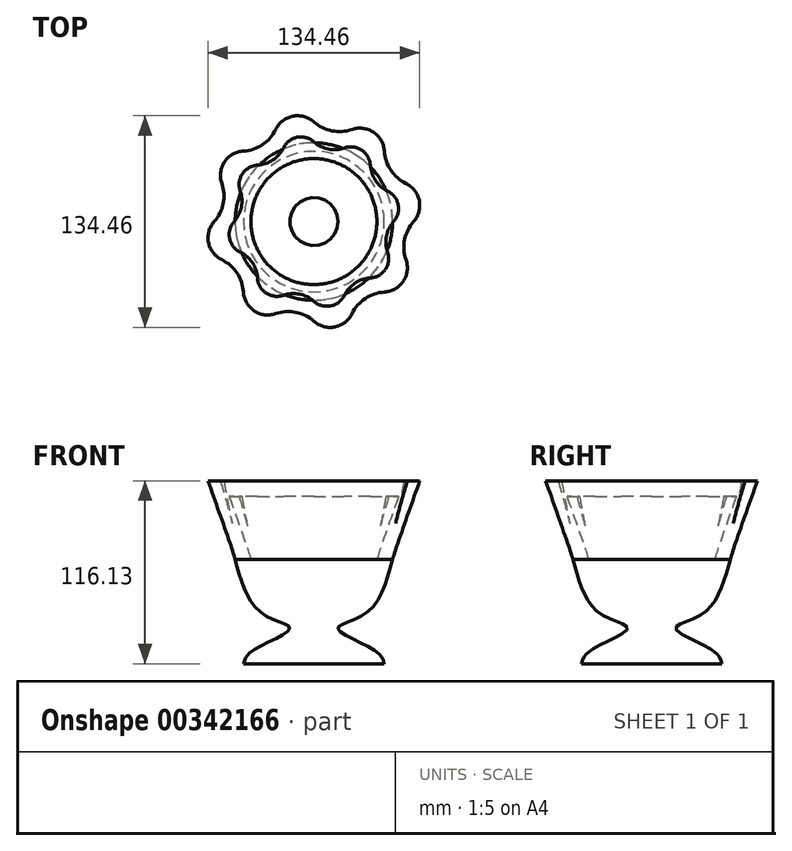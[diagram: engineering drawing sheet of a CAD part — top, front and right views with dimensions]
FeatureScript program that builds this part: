
annotation { "Feature Type Name" : "Feature", "Feature Type Description" : "" }
export const myFeature = defineFeature(function(context is Context, id is Id, definition is map)
    precondition{}
    {
        {
            var Q0;
            Q0=qCreatedBy(makeId("Top.planeOp"),FACE);
            var sketch = newSketch(context, id + "F0", { "sketchPlane" : qUnion([Q0])});
            skCircle(sketch, "E0", {"center": v(0, 0) * mm, "radius": 50 * mm});
            skSolve(sketch);
        }
        {
            var Q0;
            Q0=qCreatedBy(makeId("Front.planeOp"),FACE);
            var sketch = newSketch(context, id + "F1", { "sketchPlane" : qUnion([Q0])});
            skFitSpline(sketch, "E1", {"points": [v(-50, 0) * mm, v(-32.23, -34.65) * mm, v(-15.28, -43.73) * mm, v(-39.5, -58.26) * mm, v(-44.64, -66.13) * mm], "startDerivative": vector(35.94, -126.86) * mm, "endDerivative": vector(-11.41, -46.65) * mm});
            skLineSegment(sketch, "E2", {"start": v(-44.64, -66.13) * mm, "end": v(0, -66.13) * mm});
            skSolve(sketch);
        }
        {
            var Q0;
            Q0 = qSketchRegion(id + "F1", true);
            var Q1;
            Q1=sQuery(id+"F1.wireOp",EDGE,"E1");
            var Q2;
            Q2=sQuery(id+"F0.wireOp",EDGE,"E0");
            revolve(context, id + "F2", {"bodyType" : ToolBodyType.SURFACE, "entities" : qUnion([Q0]), "surfaceEntities" : qUnion([Q1]), "axis" : qUnion([Q2]), "revolveType" : RevolveType.FULL});
        }
        {
            var Q0;
            Q0=qCreatedBy(makeId("Top.planeOp"),FACE);
            var sketch = newSketch(context, id + "F3", { "sketchPlane" : qUnion([Q0])});
            skLineSegment(sketch, "E3", {"start": v(0, 0) * mm, "end": v(0, 63.32) * mm});
            skLineSegment(sketch, "E4.1.0", {"start": v(0, 0) * mm, "end": v(-24.23, 58.5) * mm});
            skLineSegment(sketch, "E4.2.0", {"start": v(0, 0) * mm, "end": v(-44.77, 44.77) * mm});
            skLineSegment(sketch, "E4.3.0", {"start": v(0, 0) * mm, "end": v(-58.5, 24.23) * mm});
            skLineSegment(sketch, "E4.4.0", {"start": v(0, 0) * mm, "end": v(-63.32, 0) * mm});
            skLineSegment(sketch, "E4.5.0", {"start": v(0, 0) * mm, "end": v(-58.5, -24.23) * mm});
            skLineSegment(sketch, "E4.6.0", {"start": v(0, 0) * mm, "end": v(-44.77, -44.77) * mm});
            skLineSegment(sketch, "E4.7.0", {"start": v(0, 0) * mm, "end": v(-24.23, -58.5) * mm});
            skLineSegment(sketch, "E4.8.0", {"start": v(0, 0) * mm, "end": v(0, -63.32) * mm});
            skLineSegment(sketch, "E4.9.0", {"start": v(0, 0) * mm, "end": v(24.23, -58.5) * mm});
            skLineSegment(sketch, "E4.10.0", {"start": v(0, 0) * mm, "end": v(44.77, -44.77) * mm});
            skLineSegment(sketch, "E4.11.0", {"start": v(0, 0) * mm, "end": v(58.5, -24.23) * mm});
            skLineSegment(sketch, "E4.12.0", {"start": v(0, 0) * mm, "end": v(63.32, 0) * mm});
            skLineSegment(sketch, "E4.13.0", {"start": v(0, 0) * mm, "end": v(58.5, 24.23) * mm});
            skLineSegment(sketch, "E4.14.0", {"start": v(0, 0) * mm, "end": v(44.77, 44.77) * mm});
            skLineSegment(sketch, "E4.15.0", {"start": v(0, 0) * mm, "end": v(24.23, 58.5) * mm});
            skPoint(sketch, "E4.center", {"position": v(0, 0) * mm});
            skArc(sketch, "E5", {"start": v(0, 63.32) * mm, "mid": v(-13.31, 66.93) * mm, "end": v(-24.23, 58.5) * mm});
            skArc(sketch, "E6", {"start": v(0, 63.32) * mm, "mid": v(11.46, 57.62) * mm, "end": v(24.23, 58.5) * mm});
            skArc(sketch, "E7.1.0", {"start": v(-44.77, 44.77) * mm, "mid": v(-56.74, 37.91) * mm, "end": v(-58.5, 24.23) * mm});
            skArc(sketch, "E7.1.1", {"start": v(-44.77, 44.77) * mm, "mid": v(-32.64, 48.85) * mm, "end": v(-24.23, 58.5) * mm});
            skArc(sketch, "E7.2.0", {"start": v(-63.32, 0) * mm, "mid": v(-66.93, -13.31) * mm, "end": v(-58.5, -24.23) * mm});
            skArc(sketch, "E7.2.1", {"start": v(-63.32, 0) * mm, "mid": v(-57.62, 11.46) * mm, "end": v(-58.5, 24.23) * mm});
            skArc(sketch, "E7.3.0", {"start": v(-44.77, -44.77) * mm, "mid": v(-37.91, -56.74) * mm, "end": v(-24.23, -58.5) * mm});
            skArc(sketch, "E7.3.1", {"start": v(-44.77, -44.77) * mm, "mid": v(-48.85, -32.64) * mm, "end": v(-58.5, -24.23) * mm});
            skArc(sketch, "E7.4.0", {"start": v(0, -63.32) * mm, "mid": v(13.31, -66.93) * mm, "end": v(24.23, -58.5) * mm});
            skArc(sketch, "E7.4.1", {"start": v(0, -63.32) * mm, "mid": v(-11.46, -57.62) * mm, "end": v(-24.23, -58.5) * mm});
            skArc(sketch, "E7.5.0", {"start": v(44.77, -44.77) * mm, "mid": v(56.74, -37.91) * mm, "end": v(58.5, -24.23) * mm});
            skArc(sketch, "E7.5.1", {"start": v(44.77, -44.77) * mm, "mid": v(32.64, -48.85) * mm, "end": v(24.23, -58.5) * mm});
            skArc(sketch, "E7.6.0", {"start": v(63.32, 0) * mm, "mid": v(66.93, 13.31) * mm, "end": v(58.5, 24.23) * mm});
            skArc(sketch, "E7.6.1", {"start": v(63.32, 0) * mm, "mid": v(57.62, -11.46) * mm, "end": v(58.5, -24.23) * mm});
            skArc(sketch, "E7.7.0", {"start": v(44.77, 44.77) * mm, "mid": v(37.91, 56.74) * mm, "end": v(24.23, 58.5) * mm});
            skArc(sketch, "E7.7.1", {"start": v(44.77, 44.77) * mm, "mid": v(48.85, 32.64) * mm, "end": v(58.5, 24.23) * mm});
            skSolve(sketch);
        }
        {
            var Q0;
            Q0=qCreatedBy(makeId("Top.planeOp"),FACE);
            cPlane(context, id + "F4", {"entities" : qUnion([Q0]), "cplaneType" : CPlaneType.OFFSET, "offset" : 50 * mm, "width" : 152.4 * mm, "height" : 152.4 * mm});
        }
        {
            var Q0;
            Q0=qCreatedBy(id+"F4.planeOp",FACE);
            var sketch = newSketch(context, id + "F5", { "sketchPlane" : qUnion([Q0])});
            skLineSegment(sketch, "E8.0", {"start": v(0, 0) * mm, "end": v(0, 63.32) * mm, "construction": true});
            skLineSegment(sketch, "E8.1", {"start": v(0, 0) * mm, "end": v(-24.23, 58.5) * mm, "construction": true});
            skLineSegment(sketch, "E8.2", {"start": v(0, 0) * mm, "end": v(-44.77, 44.77) * mm, "construction": true});
            skLineSegment(sketch, "E8.3", {"start": v(0, 0) * mm, "end": v(-58.5, 24.23) * mm, "construction": true});
            skLineSegment(sketch, "E8.4", {"start": v(0, 0) * mm, "end": v(-63.32, 0) * mm, "construction": true});
            skLineSegment(sketch, "E8.5", {"start": v(0, 0) * mm, "end": v(-58.5, -24.23) * mm, "construction": true});
            skLineSegment(sketch, "E8.6", {"start": v(0, 0) * mm, "end": v(-44.77, -44.77) * mm, "construction": true});
            skLineSegment(sketch, "E8.7", {"start": v(0, 0) * mm, "end": v(-24.23, -58.5) * mm, "construction": true});
            skLineSegment(sketch, "E8.8", {"start": v(0, 0) * mm, "end": v(0, -63.32) * mm, "construction": true});
            skLineSegment(sketch, "E8.9", {"start": v(0, 0) * mm, "end": v(24.23, -58.5) * mm, "construction": true});
            skLineSegment(sketch, "E8.10", {"start": v(0, 0) * mm, "end": v(44.77, -44.77) * mm, "construction": true});
            skLineSegment(sketch, "E8.11", {"start": v(0, 0) * mm, "end": v(58.5, -24.23) * mm, "construction": true});
            skLineSegment(sketch, "E8.12", {"start": v(0, 0) * mm, "end": v(63.32, 0) * mm, "construction": true});
            skLineSegment(sketch, "E8.13", {"start": v(0, 0) * mm, "end": v(58.5, 24.23) * mm, "construction": true});
            skLineSegment(sketch, "E8.14", {"start": v(0, 0) * mm, "end": v(44.77, 44.77) * mm, "construction": true});
            skLineSegment(sketch, "E8.15", {"start": v(0, 0) * mm, "end": v(24.23, 58.5) * mm, "construction": true});
            skPoint(sketch, "E8.16", {"position": v(0, 0) * mm});
            skArc(sketch, "E8.17", {"start": v(0, 63.32) * mm, "mid": v(-13.31, 66.93) * mm, "end": v(-24.23, 58.5) * mm});
            skArc(sketch, "E8.18", {"start": v(0, 63.32) * mm, "mid": v(11.46, 57.62) * mm, "end": v(24.23, 58.5) * mm});
            skArc(sketch, "E8.19", {"start": v(-44.77, 44.77) * mm, "mid": v(-56.74, 37.91) * mm, "end": v(-58.5, 24.23) * mm});
            skArc(sketch, "E8.20", {"start": v(-44.77, 44.77) * mm, "mid": v(-32.64, 48.85) * mm, "end": v(-24.23, 58.5) * mm});
            skArc(sketch, "E8.21", {"start": v(-63.32, 0) * mm, "mid": v(-66.93, -13.31) * mm, "end": v(-58.5, -24.23) * mm});
            skArc(sketch, "E8.22", {"start": v(-63.32, 0) * mm, "mid": v(-57.62, 11.46) * mm, "end": v(-58.5, 24.23) * mm});
            skArc(sketch, "E8.23", {"start": v(-44.77, -44.77) * mm, "mid": v(-37.91, -56.74) * mm, "end": v(-24.23, -58.5) * mm});
            skArc(sketch, "E8.24", {"start": v(-44.77, -44.77) * mm, "mid": v(-48.85, -32.64) * mm, "end": v(-58.5, -24.23) * mm});
            skArc(sketch, "E8.25", {"start": v(0, -63.32) * mm, "mid": v(13.31, -66.93) * mm, "end": v(24.23, -58.5) * mm});
            skArc(sketch, "E8.26", {"start": v(0, -63.32) * mm, "mid": v(-11.46, -57.62) * mm, "end": v(-24.23, -58.5) * mm});
            skArc(sketch, "E8.27", {"start": v(44.77, -44.77) * mm, "mid": v(56.74, -37.91) * mm, "end": v(58.5, -24.23) * mm});
            skArc(sketch, "E8.28", {"start": v(44.77, -44.77) * mm, "mid": v(32.64, -48.85) * mm, "end": v(24.23, -58.5) * mm});
            skArc(sketch, "E8.29", {"start": v(63.32, 0) * mm, "mid": v(66.93, 13.31) * mm, "end": v(58.5, 24.23) * mm});
            skArc(sketch, "E8.30", {"start": v(63.32, 0) * mm, "mid": v(57.62, -11.46) * mm, "end": v(58.5, -24.23) * mm});
            skArc(sketch, "E8.31", {"start": v(44.77, 44.77) * mm, "mid": v(37.91, 56.74) * mm, "end": v(24.23, 58.5) * mm});
            skArc(sketch, "E8.32", {"start": v(44.77, 44.77) * mm, "mid": v(48.85, 32.64) * mm, "end": v(58.5, 24.23) * mm});
            skPoint(sketch, "E8.33", {"position": v(0, 0) * mm});
            skSolve(sketch);
        }
        {
            var Q0;
            Q0 = qConstructionFilter(qBodyType(qCreatedBy(id + "F5" ,EDGE), BodyType.WIRE), ConstructionObject.NO);
            var Q1;
            Q1=makeQuery(id+"F2.opRevolve","SWEPT_EDGE",EDGE,{"disambiguationData":[OSD([sQuery(id+"F1.wireOp",VERTEX,"E1.start")])]});
            loft(context, id + "F6", {"bodyType" : ToolBodyType.SURFACE, "wireProfilesArray" : [{ "wireProfileEntities" : qUnion([Q0]) }, { "wireProfileEntities" : qUnion([Q1]) }]});
        }
        {
            var Q0;
            Q0=qCreatedBy(makeId("Front.planeOp"),FACE);
            var sketch = newSketch(context, id + "F7", { "sketchPlane" : qUnion([Q0])});
            skLineSegment(sketch, "E9", {"start": v(-44.64, -66.13) * mm, "end": v(0, -66.13) * mm});
            skSolve(sketch);
        }
        {
            var Q0;
            Q0 = qSketchRegion(id + "F7", true);
            var Q1;
            Q1=sQuery(id+"F7.wireOp",EDGE,"E9");
            var Q2;
            Q2=makeQuery(id+"F2.opRevolve","SWEPT_EDGE",EDGE,{"disambiguationData":[OSD([sQuery(id+"F1.wireOp",VERTEX,"E1.end")])]});
            revolve(context, id + "F8", {"bodyType" : ToolBodyType.SURFACE, "entities" : qUnion([Q0]), "surfaceEntities" : qUnion([Q1]), "axis" : qUnion([Q2]), "revolveType" : RevolveType.FULL});
        }
        {
            var Q0;
            Q0=makeQuery(id+"F6.opLoft","SWEPT_BODY",BODY,{"disambiguationData":[OSD([sQuery(id+"F1.wireOp",VERTEX,"E1.start"),sQuery(id+"F5.wireOp",EDGE,"E8.30")])]});
            var Q1;
            Q1=qCreatedBy(makeId("Origin.pointOp"),VERTEX);
            transform(context, id + "F9", {"entities" : qUnion([Q0]), "transformType" : TransformType.SCALE_UNIFORMLY, "scale" : 0.8, "scalePoint" : qUnion([Q1]), "makeCopy" : true});
        }
    });
